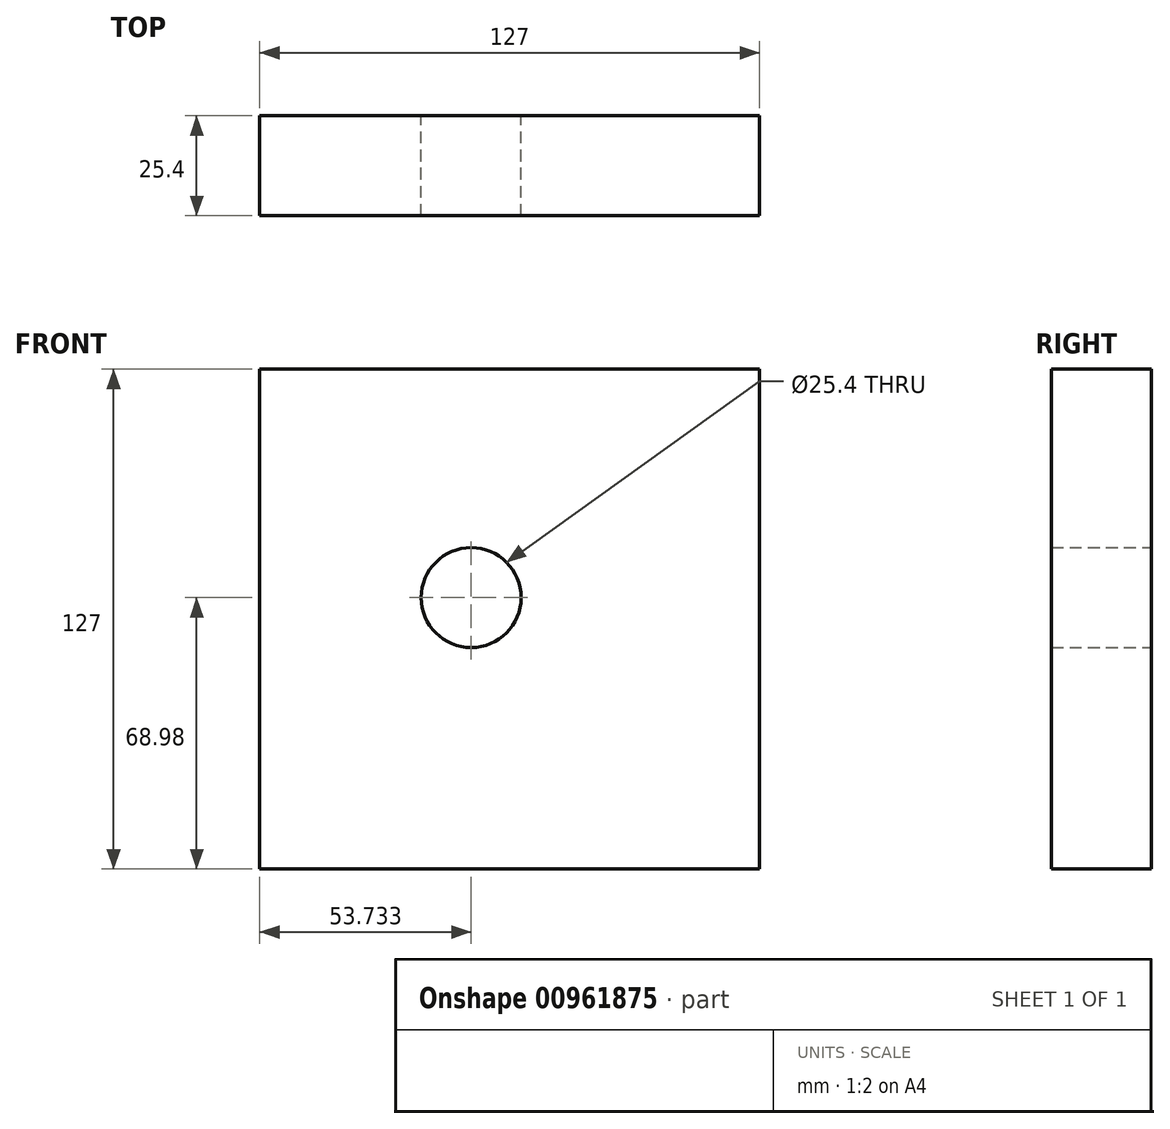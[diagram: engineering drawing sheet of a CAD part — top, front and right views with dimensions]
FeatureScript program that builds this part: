
annotation { "Feature Type Name" : "Feature", "Feature Type Description" : "" }
export const myFeature = defineFeature(function(context is Context, id is Id, definition is map)
    precondition{}
    {
        {
            var Q0;
            Q0=qCreatedBy(makeId("Front.planeOp"),FACE);
            var sketch = newSketch(context, id + "F0", { "sketchPlane" : qUnion([Q0])});
            skLineSegment(sketch, "E0.bottom", {"start": v(63.5, 58.02) * mm, "end": v(-63.5, 58.02) * mm});
            skLineSegment(sketch, "E0.top", {"start": v(63.5, -68.98) * mm, "end": v(-63.5, -68.98) * mm});
            skLineSegment(sketch, "E0.left", {"start": v(63.5, 58.02) * mm, "end": v(63.5, -68.98) * mm});
            skLineSegment(sketch, "E0.right", {"start": v(-63.5, 58.02) * mm, "end": v(-63.5, -68.98) * mm});
            skPoint(sketch, "E0.middle", {"position": v(0, -5.48) * mm});
            skSolve(sketch);
        }
        {
            var Q0;
            Q0 = qSketchRegion(id + "F0", true);
            extrude(context, id + "F1", {"entities" : qUnion([Q0]), "depth" : 25.4 * mm, "offsetDistance" : 25.4 * mm});
        }
        {
            var Q0;
            Q0=qCreatedBy(makeId("Front.planeOp"),FACE);
            var sketch = newSketch(context, id + "F2", { "sketchPlane" : qUnion([Q0])});
            skPoint(sketch, "E1", {"position": v(0, 0) * mm});
            skPoint(sketch, "E2", {"position": v(-9.77, 0) * mm});
            skSolve(sketch);
        }
        {
            var Q0;
            Q0=sQuery(id+"F2.wireOp",VERTEX,"E2");
            var Q1;
            Q1=makeQuery(id+"F1.opExtrude","SWEPT_BODY",BODY,{"disambiguationData":[OSD([sQuery(id+"F0.wireOp",EDGE,"E0.bottom"),sQuery(id+"F0.wireOp",EDGE,"E0.top"),sQuery(id+"F0.wireOp",EDGE,"E0.left"),sQuery(id+"F0.wireOp",EDGE,"E0.right")])]});
            hole(context, id + "F3", {"style" : HoleStyle.SIMPLE, "endStyle" : HoleEndStyle.THROUGH, "oppositeDirection" : true, "holeDiameter" : 25.4 * mm, "majorDiameter" : 6.35 * mm, "isTappedThrough" : true, "tappedDepth" : 12.7 * mm, "tapClearance" : 3, "locations" : qUnion([Q0]), "scope" : qUnion([Q1])});
        }
    });
